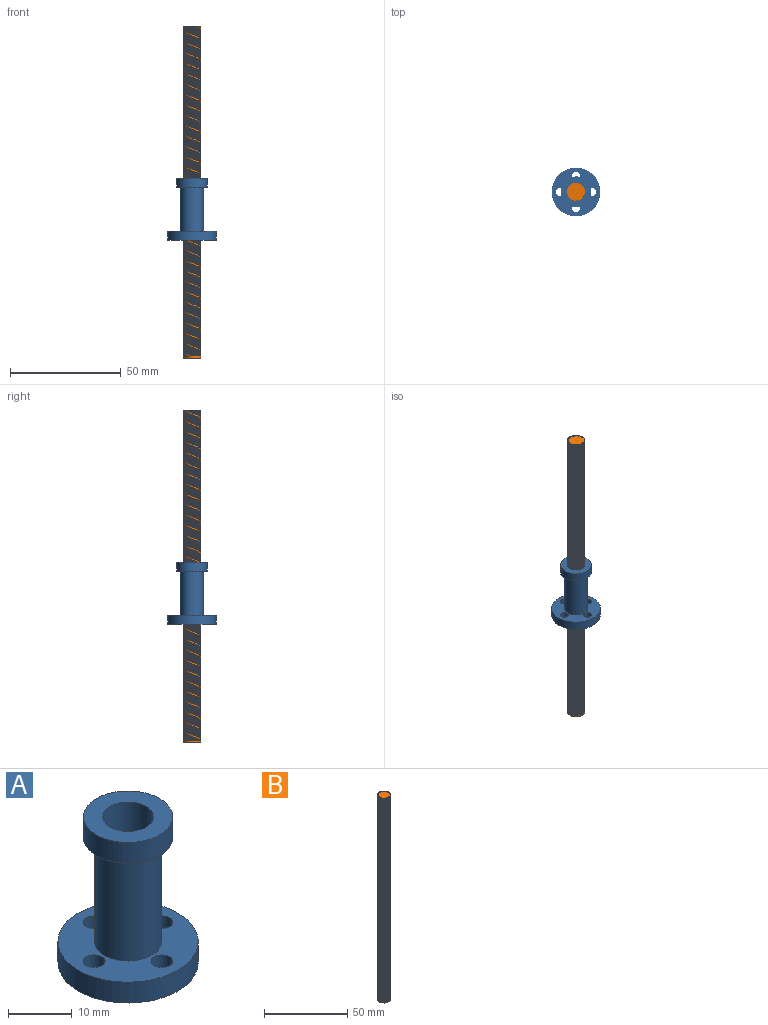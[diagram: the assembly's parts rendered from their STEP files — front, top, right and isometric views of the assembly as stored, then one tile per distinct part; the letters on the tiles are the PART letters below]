
ASSEMBLY  parts=2 mates=1
PART A: 12 faces, bbox 22x22x28 mm
  f0: cylinder r=1.7mm len=4mm, axis (0,0,-1), area 42.7mm2, adj f5,f7
  f1: cylinder r=1.7mm len=4mm, axis (0,0,-1), area 42.7mm2, adj f5,f7
  f2: cylinder r=1.7mm len=4mm, axis (0,0,-1), area 42.7mm2, adj f5,f7
  f3: plane 14x14mm, normal (0,0,1), area 103.7mm2, adj f4,f10
  f4: cylinder r=4mm len=28mm, axis (0,0,1), area 703.7mm2, adj f3,f5
  f5: plane 22x22mm, normal (0,0,-1), area 293.6mm2, adj f0,f1,f2,f4,f6,f11
  f6: cylinder r=11mm len=22mm, axis (0,0,1), area 276.5mm2, adj f5,f7
  f7: plane 22x22mm, normal (0,0,1), area 257.2mm2, adj f0,f1,f2,f6,f8,f11
  f8: cylinder r=5.25mm len=20mm, axis (0,0,1), area 659.7mm2, adj f7,f9
  f9: plane 14x14mm, normal (0,0,-1), area 67.3mm2, adj f8,f10
  f10: cylinder r=7mm len=14mm, axis (0,0,1), area 175.9mm2, adj f3,f9
  f11: cylinder r=1.7mm len=4mm, axis (0,0,-1), area 42.7mm2, adj f5,f7
PART B: 157 faces, bbox 9x10.4x150 mm
  f0: cylinder r=4mm len=8mm, axis (0,0,-1), area 17.1mm2, adj f1,f152,f153,f155
  f1: cylinder r=4mm len=8mm, axis (0,0,-1), area 12.6mm2, adj f0,f2,f154,f155
  f2: cylinder r=4mm len=8mm, axis (0,0,-1), area 12.6mm2, adj f1,f3,f154,f155
  f3: cylinder r=4mm len=8mm, axis (0,0,-1), area 12.6mm2, adj f2,f4,f154,f155
  f4: cylinder r=4mm len=8mm, axis (0,0,-1), area 12.6mm2, adj f3,f5,f154,f155
  f5: cylinder r=4mm len=8mm, axis (0,0,-1), area 12.6mm2, adj f4,f6,f154,f155
  f6: cylinder r=4mm len=8mm, axis (0,0,-1), area 12.6mm2, adj f5,f7,f154,f155
  f7: cylinder r=4mm len=8mm, axis (0,0,-1), area 12.6mm2, adj f6,f8,f154,f155
  f8: cylinder r=4mm len=8mm, axis (0,0,-1), area 12.6mm2, adj f7,f9,f154,f155
  f9: cylinder r=4mm len=8mm, axis (0,0,-1), area 12.6mm2, adj f8,f10,f154,f155
  f10: cylinder r=4mm len=8mm, axis (0,0,-1), area 12.6mm2, adj f9,f11,f154,f155
  f11: cylinder r=4mm len=8mm, axis (0,0,-1), area 12.6mm2, adj f10,f12,f154,f155
  f12: cylinder r=4mm len=8mm, axis (0,0,-1), area 12.6mm2, adj f11,f13,f154,f155
  f13: cylinder r=4mm len=8mm, axis (0,0,-1), area 12.6mm2, adj f12,f14,f154,f155
  f14: cylinder r=4mm len=8mm, axis (0,0,-1), area 12.6mm2, adj f13,f15,f154,f155
  f15: cylinder r=4mm len=8mm, axis (0,0,-1), area 12.6mm2, adj f14,f16,f154,f155
  f16: cylinder r=4mm len=8mm, axis (0,0,-1), area 12.6mm2, adj f15,f17,f154,f155
  f17: cylinder r=4mm len=8mm, axis (0,0,-1), area 12.6mm2, adj f16,f18,f154,f155
  f18: cylinder r=4mm len=8mm, axis (0,0,-1), area 12.6mm2, adj f17,f19,f154,f155
  f19: cylinder r=4mm len=8mm, axis (0,0,-1), area 12.6mm2, adj f18,f20,f154,f155
  f20: cylinder r=4mm len=8mm, axis (0,0,-1), area 12.6mm2, adj f19,f21,f154,f155
  f21: cylinder r=4mm len=8mm, axis (0,0,-1), area 12.6mm2, adj f20,f22,f154,f155
  f22: cylinder r=4mm len=8mm, axis (0,0,-1), area 12.6mm2, adj f21,f23,f154,f155
  f23: cylinder r=4mm len=8mm, axis (0,0,-1), area 12.6mm2, adj f22,f24,f154,f155
  f24: cylinder r=4mm len=8mm, axis (0,0,-1), area 12.6mm2, adj f23,f25,f154,f155
  f25: cylinder r=4mm len=8mm, axis (0,0,-1), area 12.6mm2, adj f24,f26,f154,f155
  f26: cylinder r=4mm len=8mm, axis (0,0,-1), area 12.6mm2, adj f25,f27,f154,f155
  f27: cylinder r=4mm len=8mm, axis (0,0,-1), area 12.6mm2, adj f26,f28,f154,f155
  f28: cylinder r=4mm len=8mm, axis (0,0,-1), area 12.6mm2, adj f27,f29,f154,f155
  f29: cylinder r=4mm len=8mm, axis (0,0,-1), area 12.6mm2, adj f28,f30,f154,f155
  f30: cylinder r=4mm len=8mm, axis (0,0,-1), area 12.6mm2, adj f29,f31,f154,f155
  f31: cylinder r=4mm len=8mm, axis (0,0,-1), area 12.6mm2, adj f30,f32,f154,f155
  f32: cylinder r=4mm len=8mm, axis (0,0,-1), area 12.6mm2, adj f31,f33,f154,f155
  f33: cylinder r=4mm len=8mm, axis (0,0,-1), area 12.6mm2, adj f32,f34,f154,f155
  f34: cylinder r=4mm len=8mm, axis (0,0,-1), area 12.6mm2, adj f33,f35,f154,f155
  f35: cylinder r=4mm len=8mm, axis (0,0,-1), area 12.6mm2, adj f34,f36,f154,f155
  f36: cylinder r=4mm len=8mm, axis (0,0,-1), area 12.6mm2, adj f35,f37,f154,f155
  f37: cylinder r=4mm len=8mm, axis (0,0,-1), area 12.6mm2, adj f36,f38,f154,f155
  f38: cylinder r=4mm len=8mm, axis (0,0,-1), area 12.6mm2, adj f37,f39,f154,f155
  f39: cylinder r=4mm len=8mm, axis (0,0,-1), area 12.6mm2, adj f38,f40,f154,f155
  f40: cylinder r=4mm len=8mm, axis (0,0,-1), area 12.6mm2, adj f39,f41,f154,f155
  f41: cylinder r=4mm len=8mm, axis (0,0,-1), area 12.6mm2, adj f40,f42,f154,f155
  f42: cylinder r=4mm len=8mm, axis (0,0,-1), area 12.6mm2, adj f41,f43,f154,f155
  f43: cylinder r=4mm len=8mm, axis (0,0,-1), area 12.6mm2, adj f42,f44,f154,f155
  f44: cylinder r=4mm len=8mm, axis (0,0,-1), area 12.6mm2, adj f43,f45,f154,f155
  f45: cylinder r=4mm len=8mm, axis (0,0,-1), area 12.6mm2, adj f44,f46,f154,f155
  f46: cylinder r=4mm len=8mm, axis (0,0,-1), area 12.6mm2, adj f45,f47,f154,f155
  f47: cylinder r=4mm len=8mm, axis (0,0,-1), area 12.6mm2, adj f46,f48,f154,f155
  f48: cylinder r=4mm len=8mm, axis (0,0,-1), area 12.6mm2, adj f47,f49,f154,f155
  f49: cylinder r=4mm len=8mm, axis (0,0,-1), area 12.6mm2, adj f48,f50,f154,f155
  f50: cylinder r=4mm len=8mm, axis (0,0,-1), area 12.6mm2, adj f49,f51,f154,f155
  f51: cylinder r=4mm len=8mm, axis (0,0,-1), area 12.6mm2, adj f50,f52,f154,f155
  f52: cylinder r=4mm len=8mm, axis (0,0,-1), area 12.6mm2, adj f51,f53,f154,f155
  f53: cylinder r=4mm len=8mm, axis (0,0,-1), area 12.6mm2, adj f52,f54,f154,f155
  f54: cylinder r=4mm len=8mm, axis (0,0,-1), area 12.6mm2, adj f53,f55,f154,f155
  f55: cylinder r=4mm len=8mm, axis (0,0,-1), area 12.6mm2, adj f54,f56,f154,f155
  f56: cylinder r=4mm len=8mm, axis (0,0,-1), area 12.6mm2, adj f55,f57,f154,f155
  f57: cylinder r=4mm len=8mm, axis (0,0,-1), area 12.6mm2, adj f56,f58,f154,f155
  f58: cylinder r=4mm len=8mm, axis (0,0,-1), area 12.6mm2, adj f57,f59,f154,f155
  f59: cylinder r=4mm len=8mm, axis (0,0,-1), area 12.6mm2, adj f58,f60,f154,f155
  f60: cylinder r=4mm len=8mm, axis (0,0,-1), area 12.6mm2, adj f59,f61,f154,f155
  f61: cylinder r=4mm len=8mm, axis (0,0,-1), area 12.6mm2, adj f60,f62,f154,f155
  f62: cylinder r=4mm len=8mm, axis (0,0,-1), area 12.6mm2, adj f61,f63,f154,f155
  f63: cylinder r=4mm len=8mm, axis (0,0,-1), area 12.6mm2, adj f62,f64,f154,f155
  f64: cylinder r=4mm len=8mm, axis (0,0,-1), area 12.6mm2, adj f63,f65,f154,f155
  f65: cylinder r=4mm len=8mm, axis (0,0,-1), area 12.6mm2, adj f64,f66,f154,f155
  f66: cylinder r=4mm len=8mm, axis (0,0,-1), area 12.6mm2, adj f65,f67,f154,f155
  f67: cylinder r=4mm len=8mm, axis (0,0,-1), area 12.6mm2, adj f66,f68,f154,f155
  f68: cylinder r=4mm len=8mm, axis (0,0,-1), area 12.6mm2, adj f67,f69,f154,f155
  f69: cylinder r=4mm len=8mm, axis (0,0,-1), area 12.6mm2, adj f68,f70,f154,f155
  f70: cylinder r=4mm len=8mm, axis (0,0,-1), area 12.6mm2, adj f69,f71,f154,f155
  f71: cylinder r=4mm len=8mm, axis (0,0,-1), area 12.6mm2, adj f70,f72,f154,f155
  f72: cylinder r=4mm len=8mm, axis (0,0,-1), area 12.6mm2, adj f71,f73,f154,f155
  f73: cylinder r=4mm len=8mm, axis (0,0,-1), area 12.6mm2, adj f72,f74,f154,f155
  f74: cylinder r=4mm len=8mm, axis (0,0,-1), area 12.6mm2, adj f73,f75,f154,f155
  f75: cylinder r=4mm len=8mm, axis (0,0,-1), area 12.6mm2, adj f74,f76,f154,f155
  f76: cylinder r=4mm len=8mm, axis (0,0,-1), area 12.6mm2, adj f75,f77,f154,f155
  f77: cylinder r=4mm len=8mm, axis (0,0,-1), area 12.6mm2, adj f76,f78,f154,f155
  f78: cylinder r=4mm len=8mm, axis (0,0,-1), area 12.6mm2, adj f77,f79,f154,f155
  f79: cylinder r=4mm len=8mm, axis (0,0,-1), area 12.6mm2, adj f78,f80,f154,f155
  f80: cylinder r=4mm len=8mm, axis (0,0,-1), area 12.6mm2, adj f79,f81,f154,f155
  f81: cylinder r=4mm len=8mm, axis (0,0,-1), area 12.6mm2, adj f80,f82,f154,f155
  f82: cylinder r=4mm len=8mm, axis (0,0,-1), area 12.6mm2, adj f81,f83,f154,f155
  f83: cylinder r=4mm len=8mm, axis (0,0,-1), area 12.6mm2, adj f82,f84,f154,f155
  f84: cylinder r=4mm len=8mm, axis (0,0,-1), area 12.6mm2, adj f83,f85,f154,f155
  f85: cylinder r=4mm len=8mm, axis (0,0,-1), area 12.6mm2, adj f84,f86,f154,f155
  f86: cylinder r=4mm len=8mm, axis (0,0,-1), area 12.6mm2, adj f85,f87,f154,f155
  f87: cylinder r=4mm len=8mm, axis (0,0,-1), area 12.6mm2, adj f86,f88,f154,f155
  f88: cylinder r=4mm len=8mm, axis (0,0,-1), area 12.6mm2, adj f87,f89,f154,f155
  f89: cylinder r=4mm len=8mm, axis (0,0,-1), area 12.6mm2, adj f88,f90,f154,f155
  f90: cylinder r=4mm len=8mm, axis (0,0,-1), area 12.6mm2, adj f89,f91,f154,f155
  f91: cylinder r=4mm len=8mm, axis (0,0,-1), area 12.6mm2, adj f90,f92,f154,f155
  f92: cylinder r=4mm len=8mm, axis (0,0,-1), area 12.6mm2, adj f91,f93,f154,f155
  f93: cylinder r=4mm len=8mm, axis (0,0,-1), area 12.6mm2, adj f92,f94,f154,f155
  f94: cylinder r=4mm len=8mm, axis (0,0,-1), area 12.6mm2, adj f93,f95,f154,f155
  f95: cylinder r=4mm len=8mm, axis (0,0,-1), area 12.6mm2, adj f94,f96,f154,f155
  f96: cylinder r=4mm len=8mm, axis (0,0,-1), area 12.6mm2, adj f95,f97,f154,f155
  f97: cylinder r=4mm len=8mm, axis (0,0,-1), area 12.6mm2, adj f96,f98,f154,f155
  f98: cylinder r=4mm len=8mm, axis (0,0,-1), area 12.6mm2, adj f97,f99,f154,f155
  f99: cylinder r=4mm len=8mm, axis (0,0,-1), area 12.6mm2, adj f98,f100,f154,f155
  f100: cylinder r=4mm len=8mm, axis (0,0,-1), area 12.6mm2, adj f99,f101,f154,f155
  f101: cylinder r=4mm len=8mm, axis (0,0,-1), area 12.6mm2, adj f100,f102,f154,f155
  f102: cylinder r=4mm len=8mm, axis (0,0,-1), area 12.6mm2, adj f101,f103,f154,f155
  f103: cylinder r=4mm len=8mm, axis (0,0,-1), area 12.6mm2, adj f102,f104,f154,f155
  f104: cylinder r=4mm len=8mm, axis (0,0,-1), area 12.6mm2, adj f103,f105,f154,f155
  f105: cylinder r=4mm len=8mm, axis (0,0,-1), area 12.6mm2, adj f104,f106,f154,f155
  f106: cylinder r=4mm len=8mm, axis (0,0,-1), area 12.6mm2, adj f105,f107,f154,f155
  f107: cylinder r=4mm len=8mm, axis (0,0,-1), area 12.6mm2, adj f106,f108,f154,f155
  f108: cylinder r=4mm len=8mm, axis (0,0,-1), area 12.6mm2, adj f107,f109,f154,f155
  f109: cylinder r=4mm len=8mm, axis (0,0,-1), area 12.6mm2, adj f108,f110,f154,f155
  f110: cylinder r=4mm len=8mm, axis (0,0,-1), area 12.6mm2, adj f109,f111,f154,f155
  f111: cylinder r=4mm len=8mm, axis (0,0,-1), area 12.6mm2, adj f110,f112,f154,f155
  f112: cylinder r=4mm len=8mm, axis (0,0,-1), area 12.6mm2, adj f111,f113,f154,f155
  f113: cylinder r=4mm len=8mm, axis (0,0,-1), area 12.6mm2, adj f112,f114,f154,f155
  f114: cylinder r=4mm len=8mm, axis (0,0,-1), area 12.6mm2, adj f113,f115,f154,f155
  f115: cylinder r=4mm len=8mm, axis (0,0,-1), area 12.6mm2, adj f114,f116,f154,f155
  f116: cylinder r=4mm len=8mm, axis (0,0,-1), area 12.6mm2, adj f115,f117,f154,f155
  f117: cylinder r=4mm len=8mm, axis (0,0,-1), area 12.6mm2, adj f116,f118,f154,f155
  f118: cylinder r=4mm len=8mm, axis (0,0,-1), area 12.6mm2, adj f117,f119,f154,f155
  f119: cylinder r=4mm len=8mm, axis (0,0,-1), area 12.6mm2, adj f118,f120,f154,f155
  f120: cylinder r=4mm len=8mm, axis (0,0,-1), area 12.6mm2, adj f119,f121,f154,f155
  f121: cylinder r=4mm len=8mm, axis (0,0,-1), area 12.6mm2, adj f120,f122,f154,f155
  f122: cylinder r=4mm len=8mm, axis (0,0,-1), area 12.6mm2, adj f121,f123,f154,f155
  f123: cylinder r=4mm len=8mm, axis (0,0,-1), area 12.6mm2, adj f122,f124,f154,f155
  f124: cylinder r=4mm len=8mm, axis (0,0,-1), area 12.6mm2, adj f123,f125,f154,f155
  f125: cylinder r=4mm len=8mm, axis (0,0,-1), area 12.6mm2, adj f124,f126,f154,f155
  f126: cylinder r=4mm len=8mm, axis (0,0,-1), area 12.6mm2, adj f125,f127,f154,f155
  f127: cylinder r=4mm len=8mm, axis (0,0,-1), area 12.6mm2, adj f126,f128,f154,f155
  f128: cylinder r=4mm len=8mm, axis (0,0,-1), area 12.6mm2, adj f127,f129,f154,f155
  f129: cylinder r=4mm len=8mm, axis (0,0,-1), area 12.6mm2, adj f128,f130,f154,f155
  f130: cylinder r=4mm len=8mm, axis (0,0,-1), area 12.6mm2, adj f129,f131,f154,f155
  f131: cylinder r=4mm len=8mm, axis (0,0,-1), area 12.6mm2, adj f130,f132,f154,f155
  f132: cylinder r=4mm len=8mm, axis (0,0,-1), area 12.6mm2, adj f131,f133,f154,f155
  f133: cylinder r=4mm len=8mm, axis (0,0,-1), area 12.6mm2, adj f132,f134,f154,f155
  f134: cylinder r=4mm len=8mm, axis (0,0,-1), area 12.6mm2, adj f133,f135,f154,f155
  f135: cylinder r=4mm len=8mm, axis (0,0,-1), area 12.6mm2, adj f134,f136,f154,f155
  f136: cylinder r=4mm len=8mm, axis (0,0,-1), area 12.6mm2, adj f135,f137,f154,f155
  f137: cylinder r=4mm len=8mm, axis (0,0,-1), area 12.6mm2, adj f136,f138,f154,f155
  f138: cylinder r=4mm len=8mm, axis (0,0,-1), area 12.6mm2, adj f137,f139,f154,f155
  f139: cylinder r=4mm len=8mm, axis (0,0,-1), area 12.6mm2, adj f138,f140,f154,f155
  f140: cylinder r=4mm len=8mm, axis (0,0,-1), area 12.6mm2, adj f139,f141,f154,f155
  f141: cylinder r=4mm len=8mm, axis (0,0,-1), area 12.6mm2, adj f140,f142,f154,f155
  f142: cylinder r=4mm len=8mm, axis (0,0,-1), area 12.6mm2, adj f141,f143,f154,f155
  f143: cylinder r=4mm len=8mm, axis (0,0,-1), area 12.6mm2, adj f142,f144,f154,f155
  f144: cylinder r=4mm len=8mm, axis (0,0,-1), area 12.6mm2, adj f143,f145,f154,f155
  f145: cylinder r=4mm len=8mm, axis (0,0,-1), area 12.6mm2, adj f144,f146,f154,f155
  f146: cylinder r=4mm len=8mm, axis (0,0,-1), area 12.6mm2, adj f145,f147,f154,f155
  f147: cylinder r=4mm len=8mm, axis (0,0,-1), area 12.6mm2, adj f146,f148,f154,f155
  f148: cylinder r=4mm len=8mm, axis (0,0,-1), area 12.6mm2, adj f147,f149,f154,f155
  f149: cylinder r=4mm len=8mm, axis (0,0,-1), area 12.2mm2, adj f148,f150,f151,f154,f155
  f150: cylinder r=4mm len=5.62mm, axis (0,0,-1), area 1.3mm2, adj f149,f151,f154
  f151: plane 7.66x7.5mm, normal (0,0,1), area 44.4mm2, adj f149,f150,f154,f155,f156
  f152: plane 8x8mm, normal (0,0,-1), area 50.3mm2, adj f0
  f153: plane 0.5x0.5mm, normal (0,1,0), area 0.3mm2, adj f0,f154,f155,f156
  f154: bspline ~149.33x10.39mm, area 1754.3mm2, adj f1,f2,f3,f4,f5,f6,f7,f8
  f155: bspline ~149.83x10.39mm, area 1766.5mm2, adj f0,f1,f2,f3,f4,f5,f6,f7
  f156: cylinder r=3.5mm len=149.82mm, axis (0,0,-1), area -715.3mm2, adj f151,f153,f154,f155
PLACE A t=(-0.54,30.72,104.13)mm
PLACE B t=(-0.54,30.72,41.73)mm fixed
MATE slider A.f4 <-> B.f0  axis (0,0,1) through (-0.54,30.72,108.94)mm
